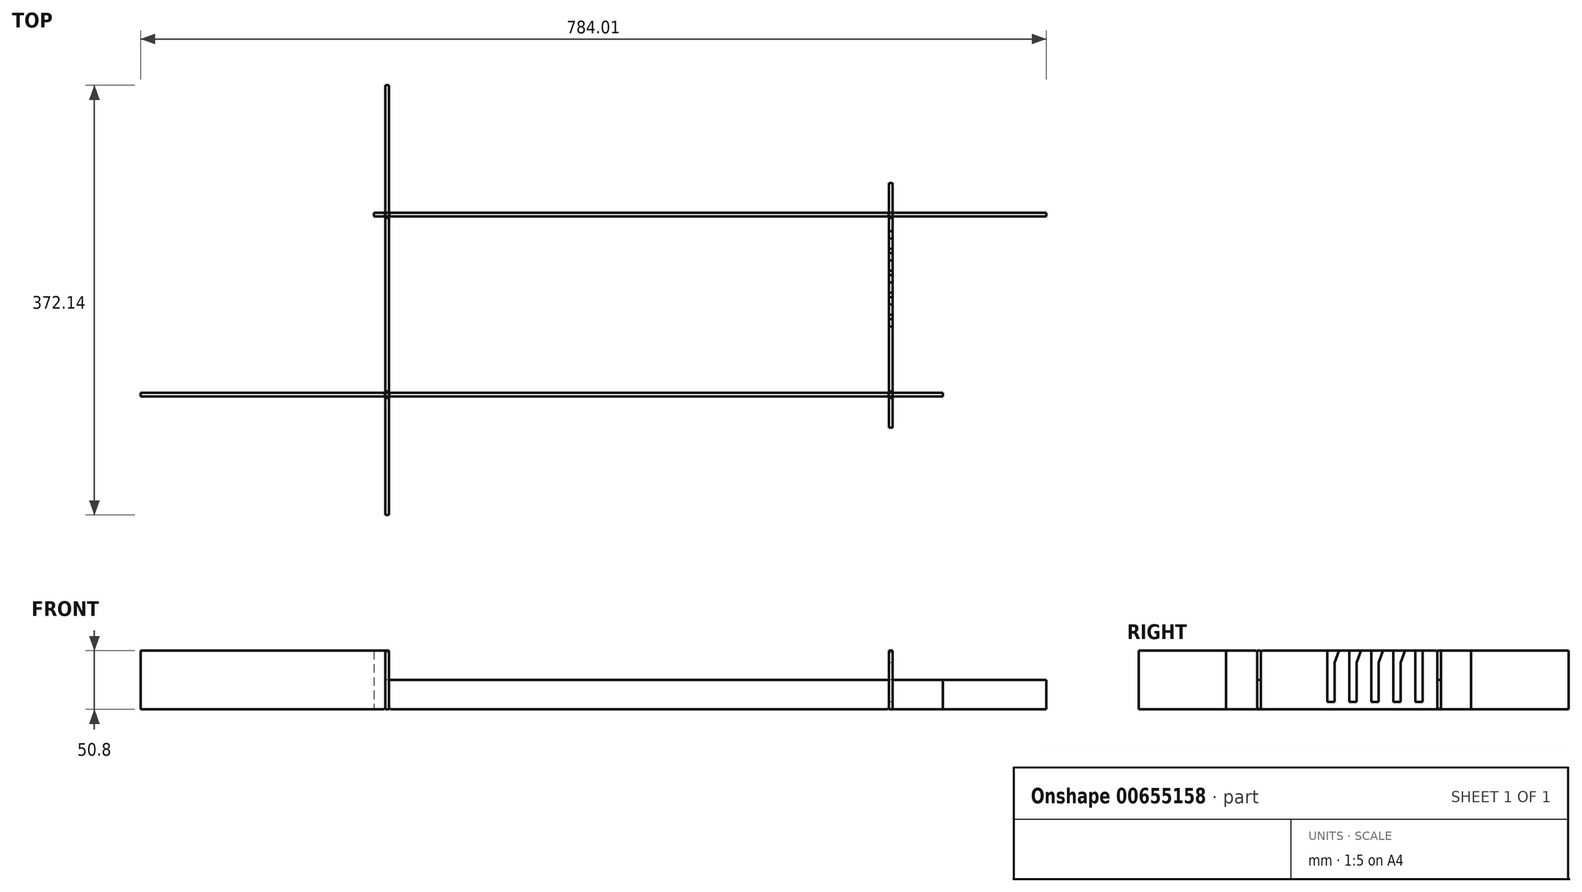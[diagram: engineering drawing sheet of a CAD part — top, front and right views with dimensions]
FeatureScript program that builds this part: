
annotation { "Feature Type Name" : "Feature", "Feature Type Description" : "" }
export const myFeature = defineFeature(function(context is Context, id is Id, definition is map)
    precondition{}
    {
        {
            var Q0;
            Q0=qCreatedBy(makeId("Top.planeOp"),FACE);
            var sketch = newSketch(context, id + "F0", { "sketchPlane" : qUnion([Q0])});
            skLineSegment(sketch, "E0", {"start": v(-96.66, -0.18) * mm, "end": v(55.66, 4.68) * mm, "construction": true});
            skLineSegment(sketch, "E1.bottom", {"start": v(-88.9, 247.87) * mm, "end": v(-85.73, 247.87) * mm});
            skLineSegment(sketch, "E1.top", {"start": v(-88.9, -124.27) * mm, "end": v(-85.72, -124.27) * mm});
            skLineSegment(sketch, "E1.left", {"start": v(-88.9, 247.87) * mm, "end": v(-88.9, -124.27) * mm});
            skLineSegment(sketch, "E1.right", {"start": v(-85.73, 247.87) * mm, "end": v(-85.72, -124.27) * mm});
            skLineSegment(sketch, "E2.bottom", {"start": v(-300.84, -18.6) * mm, "end": v(393.7, -18.6) * mm});
            skLineSegment(sketch, "E2.top", {"start": v(-300.84, -21.78) * mm, "end": v(393.7, -21.78) * mm});
            skLineSegment(sketch, "E2.left", {"start": v(-300.84, -18.6) * mm, "end": v(-300.84, -21.78) * mm});
            skLineSegment(sketch, "E2.right", {"start": v(393.7, -18.6) * mm, "end": v(393.7, -21.78) * mm});
            skLineSegment(sketch, "E3.bottom", {"start": v(483.17, 134.22) * mm, "end": v(-98.96, 134.22) * mm});
            skLineSegment(sketch, "E3.top", {"start": v(483.17, 137.4) * mm, "end": v(-98.96, 137.4) * mm});
            skLineSegment(sketch, "E3.left", {"start": v(483.17, 134.22) * mm, "end": v(483.17, 137.4) * mm});
            skLineSegment(sketch, "E3.right", {"start": v(-98.96, 134.22) * mm, "end": v(-98.96, 137.4) * mm});
            skLineSegment(sketch, "E4.bottom", {"start": v(350.04, -48.6) * mm, "end": v(346.87, -48.6) * mm});
            skLineSegment(sketch, "E4.top", {"start": v(350.04, 163.24) * mm, "end": v(346.87, 163.24) * mm});
            skLineSegment(sketch, "E4.left", {"start": v(350.04, -48.6) * mm, "end": v(350.04, 163.24) * mm});
            skLineSegment(sketch, "E4.right", {"start": v(346.87, -48.6) * mm, "end": v(346.87, 163.24) * mm});
            skSolve(sketch);
        }
        {
            var Q0;
            {var subQ0=sQuery(id+"F0.wireOp",EDGE,"E1.bottom");Q0=makeQuery(id+"F0.imprint","IMPRINT",FACE,{"disambiguationData":[TD([[makeQuery(id+"F0.imprint","IMPRINT",EDGE,{"derivedFrom":subQ0}),-1.0]])]});}
            var Q1;
            {var subQ0=sQuery(id+"F0.wireOp",EDGE,"E1.top");Q1=makeQuery(id+"F0.imprint","IMPRINT",FACE,{"disambiguationData":[TD([[makeQuery(id+"F0.imprint","IMPRINT",EDGE,{"derivedFrom":subQ0}),1.0]])]});}
            var Q2;
            {var subQ0=sQuery(id+"F0.wireOp",EDGE,"E2.bottom");var subQ1=sQuery(id+"F0.wireOp",EDGE,"E1.left");var subQ2=makeQuery(id+"F0.imprint","INTERSECT",VERTEX,{"derivedFrom":[subQ1,subQ0]});Q2=makeQuery(id+"F0.imprint","IMPRINT",FACE,{"disambiguationData":[TD([[makeQuery(id+"F0.imprint","IMPRINT",EDGE,{"disambiguationData":[TD([[subQ2,-1.0]])],"derivedFrom":subQ1}),1.0]])]});}
            var Q3;
            {var subQ0=sQuery(id+"F0.wireOp",EDGE,"E3.top");var subQ1=sQuery(id+"F0.wireOp",EDGE,"E1.left");var subQ2=makeQuery(id+"F0.imprint","INTERSECT",VERTEX,{"derivedFrom":[subQ1,subQ0]});Q3=makeQuery(id+"F0.imprint","IMPRINT",FACE,{"disambiguationData":[TD([[makeQuery(id+"F0.imprint","IMPRINT",EDGE,{"disambiguationData":[TD([[subQ2,-1.0]])],"derivedFrom":subQ1}),1.0]])]});}
            var Q4;
            {var subQ0=sQuery(id+"F0.wireOp",EDGE,"E3.bottom");var subQ1=sQuery(id+"F0.wireOp",EDGE,"E1.left");var subQ2=makeQuery(id+"F0.imprint","INTERSECT",VERTEX,{"derivedFrom":[subQ1,subQ0]});Q4=makeQuery(id+"F0.imprint","IMPRINT",FACE,{"disambiguationData":[TD([[makeQuery(id+"F0.imprint","IMPRINT",EDGE,{"disambiguationData":[TD([[subQ2,-1.0]])],"derivedFrom":subQ1}),1.0]])]});}
            extrude(context, id + "F1", {"entities" : qUnion([Q0, Q1, Q2, Q3, Q4]), "depth" : 50.8 * mm, "offsetDistance" : 25.4 * mm});
        }
        {
            var Q0;
            {var subQ5=sQuery(id+"F0.wireOp",EDGE,"E2.left");Q0=makeQuery(id+"F0.imprint","IMPRINT",FACE,{"disambiguationData":[TD([[makeQuery(id+"F0.imprint","IMPRINT",EDGE,{"derivedFrom":subQ5}),1.0]])]});}
            var Q1;
            {var subQ0=sQuery(id+"F0.wireOp",EDGE,"E2.bottom");var subQ1=sQuery(id+"F0.wireOp",EDGE,"E1.right");var subQ2=makeQuery(id+"F0.imprint","INTERSECT",VERTEX,{"derivedFrom":[subQ1,subQ0]});Q1=makeQuery(id+"F0.imprint","IMPRINT",FACE,{"disambiguationData":[TD([[makeQuery(id+"F0.imprint","IMPRINT",EDGE,{"disambiguationData":[TD([[subQ2,-1.0]])],"derivedFrom":subQ1}),1.0]])]});}
            var Q2;
            {var subQ0=sQuery(id+"F0.wireOp",EDGE,"E2.bottom");var subQ1=sQuery(id+"F0.wireOp",EDGE,"E1.left");var subQ2=makeQuery(id+"F0.imprint","INTERSECT",VERTEX,{"derivedFrom":[subQ1,subQ0]});Q2=makeQuery(id+"F0.imprint","IMPRINT",FACE,{"disambiguationData":[TD([[makeQuery(id+"F0.imprint","IMPRINT",EDGE,{"disambiguationData":[TD([[subQ2,-1.0]])],"derivedFrom":subQ1}),1.0]])]});}
            var Q3;
            {var subQ0=sQuery(id+"F0.wireOp",EDGE,"E4.right");var subQ1=sQuery(id+"F0.wireOp",EDGE,"E2.bottom");var subQ2=makeQuery(id+"F0.imprint","INTERSECT",VERTEX,{"derivedFrom":[subQ1,subQ0]});Q3=makeQuery(id+"F0.imprint","IMPRINT",FACE,{"disambiguationData":[TD([[makeQuery(id+"F0.imprint","IMPRINT",EDGE,{"disambiguationData":[TD([[subQ2,-1.0]])],"derivedFrom":subQ1}),-1.0]])]});}
            var Q4;
            {var subQ0=sQuery(id+"F0.wireOp",EDGE,"E2.right");Q4=makeQuery(id+"F0.imprint","IMPRINT",FACE,{"disambiguationData":[TD([[makeQuery(id+"F0.imprint","IMPRINT",EDGE,{"derivedFrom":subQ0}),-1.0]])]});}
            extrude(context, id + "F2", {"entities" : qUnion([Q0, Q1, Q2, Q3, Q4]), "depth" : 50.8 * mm, "offsetDistance" : 25.4 * mm});
        }
        {
            var Q0;
            {var subQ5=sQuery(id+"F0.wireOp",EDGE,"E4.bottom");Q0=makeQuery(id+"F0.imprint","IMPRINT",FACE,{"disambiguationData":[TD([[makeQuery(id+"F0.imprint","IMPRINT",EDGE,{"derivedFrom":subQ5}),-1.0]])]});}
            var Q1;
            {var subQ0=sQuery(id+"F0.wireOp",EDGE,"E4.right");var subQ1=sQuery(id+"F0.wireOp",EDGE,"E2.bottom");var subQ2=makeQuery(id+"F0.imprint","INTERSECT",VERTEX,{"derivedFrom":[subQ1,subQ0]});Q1=makeQuery(id+"F0.imprint","IMPRINT",FACE,{"disambiguationData":[TD([[makeQuery(id+"F0.imprint","IMPRINT",EDGE,{"disambiguationData":[TD([[subQ2,-1.0]])],"derivedFrom":subQ1}),-1.0]])]});}
            var Q2;
            {var subQ0=sQuery(id+"F0.wireOp",EDGE,"E4.right");var subQ1=sQuery(id+"F0.wireOp",EDGE,"E2.bottom");var subQ2=makeQuery(id+"F0.imprint","INTERSECT",VERTEX,{"derivedFrom":[subQ1,subQ0]});Q2=makeQuery(id+"F0.imprint","IMPRINT",FACE,{"disambiguationData":[TD([[makeQuery(id+"F0.imprint","IMPRINT",EDGE,{"disambiguationData":[TD([[subQ2,-1.0]])],"derivedFrom":subQ1}),1.0]])]});}
            var Q3;
            {var subQ0=sQuery(id+"F0.wireOp",EDGE,"E4.left");var subQ1=sQuery(id+"F0.wireOp",EDGE,"E3.bottom");var subQ2=makeQuery(id+"F0.imprint","INTERSECT",VERTEX,{"derivedFrom":[subQ1,subQ0]});Q3=makeQuery(id+"F0.imprint","IMPRINT",FACE,{"disambiguationData":[TD([[makeQuery(id+"F0.imprint","IMPRINT",EDGE,{"disambiguationData":[TD([[subQ2,-1.0]])],"derivedFrom":subQ1}),-1.0]])]});}
            var Q4;
            {var subQ5=sQuery(id+"F0.wireOp",EDGE,"E4.top");Q4=makeQuery(id+"F0.imprint","IMPRINT",FACE,{"disambiguationData":[TD([[makeQuery(id+"F0.imprint","IMPRINT",EDGE,{"derivedFrom":subQ5}),1.0]])]});}
            extrude(context, id + "F3", {"entities" : qUnion([Q0, Q1, Q2, Q3, Q4]), "depth" : 50.8 * mm, "offsetDistance" : 25.4 * mm});
        }
        {
            var Q0;
            {var subQ0=sQuery(id+"F0.wireOp",EDGE,"E3.left");Q0=makeQuery(id+"F0.imprint","IMPRINT",FACE,{"disambiguationData":[TD([[makeQuery(id+"F0.imprint","IMPRINT",EDGE,{"derivedFrom":subQ0}),1.0]])]});}
            var Q1;
            {var subQ0=sQuery(id+"F0.wireOp",EDGE,"E3.right");Q1=makeQuery(id+"F0.imprint","IMPRINT",FACE,{"disambiguationData":[TD([[makeQuery(id+"F0.imprint","IMPRINT",EDGE,{"derivedFrom":subQ0}),-1.0]])]});}
            var Q2;
            {var subQ0=sQuery(id+"F0.wireOp",EDGE,"E3.top");var subQ1=sQuery(id+"F0.wireOp",EDGE,"E1.left");var subQ2=makeQuery(id+"F0.imprint","INTERSECT",VERTEX,{"derivedFrom":[subQ1,subQ0]});Q2=makeQuery(id+"F0.imprint","IMPRINT",FACE,{"disambiguationData":[TD([[makeQuery(id+"F0.imprint","IMPRINT",EDGE,{"disambiguationData":[TD([[subQ2,-1.0]])],"derivedFrom":subQ1}),1.0]])]});}
            var Q3;
            {var subQ0=sQuery(id+"F0.wireOp",EDGE,"E3.top");var subQ1=sQuery(id+"F0.wireOp",EDGE,"E1.right");var subQ2=makeQuery(id+"F0.imprint","INTERSECT",VERTEX,{"derivedFrom":[subQ1,subQ0]});Q3=makeQuery(id+"F0.imprint","IMPRINT",FACE,{"disambiguationData":[TD([[makeQuery(id+"F0.imprint","IMPRINT",EDGE,{"disambiguationData":[TD([[subQ2,-1.0]])],"derivedFrom":subQ1}),1.0]])]});}
            var Q4;
            {var subQ0=sQuery(id+"F0.wireOp",EDGE,"E4.left");var subQ1=sQuery(id+"F0.wireOp",EDGE,"E3.bottom");var subQ2=makeQuery(id+"F0.imprint","INTERSECT",VERTEX,{"derivedFrom":[subQ1,subQ0]});Q4=makeQuery(id+"F0.imprint","IMPRINT",FACE,{"disambiguationData":[TD([[makeQuery(id+"F0.imprint","IMPRINT",EDGE,{"disambiguationData":[TD([[subQ2,-1.0]])],"derivedFrom":subQ1}),-1.0]])]});}
            extrude(context, id + "F4", {"entities" : qUnion([Q0, Q1, Q2, Q3, Q4]), "depth" : 50.8 * mm, "offsetDistance" : 25.4 * mm});
        }
        {
            var Q0;
            Q0=makeQuery(id+"F1.opExtrude","SWEPT_FACE",FACE,{"disambiguationData":[OSD([sQuery(id+"F0.wireOp",EDGE,"E1.left")])]});
            var sketch = newSketch(context, id + "F5", { "sketchPlane" : qUnion([Q0])});
            skLineSegment(sketch, "E5.bottom", {"start": v(-137.4, 50.8) * mm, "end": v(-134.22, 50.8) * mm});
            skLineSegment(sketch, "E5.top", {"start": v(-137.4, 25.4) * mm, "end": v(-134.22, 25.4) * mm});
            skLineSegment(sketch, "E5.left", {"start": v(-137.4, 50.8) * mm, "end": v(-137.4, 25.4) * mm});
            skLineSegment(sketch, "E5.right", {"start": v(-134.22, 50.8) * mm, "end": v(-134.22, 25.4) * mm});
            skLineSegment(sketch, "E6.bottom", {"start": v(21.78, 50.8) * mm, "end": v(18.6, 50.8) * mm});
            skLineSegment(sketch, "E6.top", {"start": v(21.78, 25.4) * mm, "end": v(18.6, 25.4) * mm});
            skLineSegment(sketch, "E6.left", {"start": v(21.78, 50.8) * mm, "end": v(21.78, 25.4) * mm});
            skLineSegment(sketch, "E6.right", {"start": v(18.6, 50.8) * mm, "end": v(18.6, 25.4) * mm});
            skSolve(sketch);
        }
        {
            var Q0;
            Q0 = qSketchRegion(id + "F5", true);
            extrude(context, id + "F6", {"entities" : qUnion([Q0]), "operationType" : NewBodyOperationType.REMOVE, "endBound" : BoundingType.THROUGH_ALL, "oppositeDirection" : true, "depth" : 25.4 * mm, "offsetDistance" : 25.4 * mm});
        }
        {
            var Q0;
            Q0=makeQuery(id+"F1.opExtrude","SWEPT_BODY",BODY,{"disambiguationData":[OSD([sQuery(id+"F0.wireOp",EDGE,"E1.bottom"),sQuery(id+"F0.wireOp",EDGE,"E1.top"),sQuery(id+"F0.wireOp",EDGE,"E1.left"),sQuery(id+"F0.wireOp",EDGE,"E1.right")])]});
            var Q1;
            Q1=makeQuery(id+"F3.opExtrude","SWEPT_BODY",BODY,{"disambiguationData":[OSD([sQuery(id+"F0.wireOp",EDGE,"E4.bottom"),sQuery(id+"F0.wireOp",EDGE,"E4.top"),sQuery(id+"F0.wireOp",EDGE,"E4.left"),sQuery(id+"F0.wireOp",EDGE,"E4.right")])]});
            var Q2;
            Q2=makeQuery(id+"F2.opExtrude","SWEPT_BODY",BODY,{"disambiguationData":[OSD([sQuery(id+"F0.wireOp",EDGE,"E2.bottom"),sQuery(id+"F0.wireOp",EDGE,"E2.top"),sQuery(id+"F0.wireOp",EDGE,"E2.left"),sQuery(id+"F0.wireOp",EDGE,"E2.right")])]});
            var Q3;
            Q3=makeQuery(id+"F4.opExtrude","SWEPT_BODY",BODY,{"disambiguationData":[OSD([sQuery(id+"F0.wireOp",EDGE,"E3.bottom"),sQuery(id+"F0.wireOp",EDGE,"E3.top"),sQuery(id+"F0.wireOp",EDGE,"E3.left"),sQuery(id+"F0.wireOp",EDGE,"E3.right")])]});
            var Q4;
            Q4=makeQuery(id+"F6.boolean.opBoolean","COPY",FACE,{"disambiguationData":[TD([makeQuery(id+"F1.opExtrude","SWEPT_FACE",FACE,{"disambiguationData":[OSD([sQuery(id+"F0.wireOp",EDGE,"E1.left")])]})])],"derivedFrom":makeQuery(id+"F6.opExtrude","SWEPT_FACE",FACE,{"disambiguationData":[OSD([sQuery(id+"F5.wireOp",EDGE,"E6.top")])]})});
            var Q5;
            Q5=makeQuery(id+"F6.boolean.opBoolean","COPY",FACE,{"disambiguationData":[TD([makeQuery(id+"F1.opExtrude","SWEPT_FACE",FACE,{"disambiguationData":[OSD([sQuery(id+"F0.wireOp",EDGE,"E1.left")])]})])],"derivedFrom":makeQuery(id+"F6.opExtrude","SWEPT_FACE",FACE,{"disambiguationData":[OSD([sQuery(id+"F5.wireOp",EDGE,"E5.top")])]})});
            var Q6;
            Q6=makeQuery(id+"F6.boolean.opBoolean","COPY",FACE,{"disambiguationData":[TD([makeQuery(id+"F3.opExtrude","SWEPT_FACE",FACE,{"disambiguationData":[OSD([sQuery(id+"F0.wireOp",EDGE,"E4.left")])]})])],"derivedFrom":makeQuery(id+"F6.opExtrude","SWEPT_FACE",FACE,{"disambiguationData":[OSD([sQuery(id+"F5.wireOp",EDGE,"E6.top")])]})});
            var Q7;
            Q7=makeQuery(id+"F6.boolean.opBoolean","COPY",FACE,{"disambiguationData":[TD([makeQuery(id+"F3.opExtrude","SWEPT_FACE",FACE,{"disambiguationData":[OSD([sQuery(id+"F0.wireOp",EDGE,"E4.left")])]})])],"derivedFrom":makeQuery(id+"F6.opExtrude","SWEPT_FACE",FACE,{"disambiguationData":[OSD([sQuery(id+"F5.wireOp",EDGE,"E5.top")])]})});
            booleanBodies(context, id + "F7", {"operationType" : BooleanOperationType.SUBTRACTION, "tools" : qUnion([Q0, Q1]), "targets" : qUnion([Q2, Q3]), "offset" : true, "entitiesToOffset" : qUnion([Q4, Q5, Q6, Q7]), "offsetDistance" : 0.25 * mm, "keepTools" : true});
        }
        {
            var Q0;
            Q0=makeQuery(id+"F3.opExtrude","SWEPT_FACE",FACE,{"disambiguationData":[OSD([sQuery(id+"F0.wireOp",EDGE,"E4.right")])]});
            var sketch = newSketch(context, id + "F8", { "sketchPlane" : qUnion([Q0])});
            skLineSegment(sketch, "E7.bottom", {"start": v(-121.52, 50.8) * mm, "end": v(-115.17, 50.8) * mm});
            skLineSegment(sketch, "E7.top", {"start": v(-121.52, 6.35) * mm, "end": v(-115.17, 6.35) * mm});
            skLineSegment(sketch, "E7.left", {"start": v(-121.52, 50.8) * mm, "end": v(-121.52, 6.35) * mm});
            skLineSegment(sketch, "E7.right", {"start": v(-115.17, 50.8) * mm, "end": v(-115.17, 6.35) * mm});
            skLineSegment(sketch, "E8.1.0.0", {"start": v(-102.47, 50.8) * mm, "end": v(-102.47, 6.35) * mm});
            skLineSegment(sketch, "E8.1.0.1", {"start": v(-96.12, 50.8) * mm, "end": v(-96.12, 6.35) * mm});
            skLineSegment(sketch, "E8.1.0.2", {"start": v(-102.47, 50.8) * mm, "end": v(-96.12, 50.8) * mm});
            skLineSegment(sketch, "E8.1.0.3", {"start": v(-102.47, 6.35) * mm, "end": v(-96.12, 6.35) * mm});
            skLineSegment(sketch, "E8.2.0.0", {"start": v(-83.42, 50.8) * mm, "end": v(-83.42, 6.35) * mm});
            skLineSegment(sketch, "E8.2.0.1", {"start": v(-77.07, 50.8) * mm, "end": v(-77.07, 6.35) * mm});
            skLineSegment(sketch, "E8.2.0.2", {"start": v(-83.42, 50.8) * mm, "end": v(-77.07, 50.8) * mm});
            skLineSegment(sketch, "E8.2.0.3", {"start": v(-83.42, 6.35) * mm, "end": v(-77.07, 6.35) * mm});
            skLineSegment(sketch, "E8.direction1", {"start": v(-121.52, 6.35) * mm, "end": v(-102.47, 6.35) * mm, "construction": true});
            skLineSegment(sketch, "E9.0.3.0", {"start": v(-64.37, 50.8) * mm, "end": v(-64.37, 6.35) * mm});
            skLineSegment(sketch, "E9.3.3.0", {"start": v(-58.02, 50.8) * mm, "end": v(-58.02, 6.35) * mm});
            skLineSegment(sketch, "E9.6.3.0", {"start": v(-64.37, 50.8) * mm, "end": v(-58.02, 50.8) * mm});
            skLineSegment(sketch, "E9.9.3.0", {"start": v(-64.37, 6.35) * mm, "end": v(-58.02, 6.35) * mm});
            skLineSegment(sketch, "E9.0.4.0", {"start": v(-45.32, 50.8) * mm, "end": v(-45.32, 6.35) * mm});
            skLineSegment(sketch, "E9.3.4.0", {"start": v(-38.97, 50.8) * mm, "end": v(-38.97, 6.35) * mm});
            skLineSegment(sketch, "E9.6.4.0", {"start": v(-45.32, 50.8) * mm, "end": v(-38.97, 50.8) * mm});
            skLineSegment(sketch, "E9.9.4.0", {"start": v(-45.32, 6.35) * mm, "end": v(-38.97, 6.35) * mm});
            skSolve(sketch);
        }
        {
            var Q0;
            Q0=makeQuery(id+"F8.imprint","IMPRINT",FACE,{"disambiguationData":[TD([[makeQuery(id+"F8.imprint","IMPRINT",EDGE,{"derivedFrom":sQuery(id+"F8.wireOp",EDGE,"E7.bottom")}),1.0]])]});
            var Q1;
            Q1=makeQuery(id+"F8.imprint","IMPRINT",FACE,{"disambiguationData":[TD([[makeQuery(id+"F8.imprint","IMPRINT",EDGE,{"derivedFrom":sQuery(id+"F8.wireOp",EDGE,"E8.1.0.0")}),1.0]])]});
            var Q2;
            Q2=makeQuery(id+"F8.imprint","IMPRINT",FACE,{"disambiguationData":[TD([[makeQuery(id+"F8.imprint","IMPRINT",EDGE,{"derivedFrom":sQuery(id+"F8.wireOp",EDGE,"E8.2.0.0")}),1.0]])]});
            var Q3;
            Q3=makeQuery(id+"F8.imprint","IMPRINT",FACE,{"disambiguationData":[TD([[makeQuery(id+"F8.imprint","IMPRINT",EDGE,{"derivedFrom":sQuery(id+"F8.wireOp",EDGE,"E9.0.3.0")}),1.0]])]});
            var Q4;
            Q4=makeQuery(id+"F8.imprint","IMPRINT",FACE,{"disambiguationData":[TD([[makeQuery(id+"F8.imprint","IMPRINT",EDGE,{"derivedFrom":sQuery(id+"F8.wireOp",EDGE,"E9.0.4.0")}),1.0]])]});
            extrude(context, id + "F9", {"entities" : qUnion([Q0, Q1, Q2, Q3, Q4]), "operationType" : NewBodyOperationType.REMOVE, "endBound" : BoundingType.UP_TO_NEXT, "oppositeDirection" : true, "depth" : 25.4 * mm, "offsetDistance" : 25.4 * mm});
        }
        {
            var Q0;
            Q0=makeQuery(id+"F9.boolean.opBoolean","COPY",EDGE,{"derivedFrom":makeQuery(id+"F9.opExtrude","SWEPT_EDGE",EDGE,{"disambiguationData":[OSD([sQuery(id+"F0.wireOp",EDGE,"E4.right"),sQuery(id+"F8.wireOp",EDGE,"E7.bottom"),sQuery(id+"F8.wireOp",EDGE,"E7.left")])]})});
            var Q1;
            Q1=makeQuery(id+"F9.boolean.opBoolean","COPY",EDGE,{"derivedFrom":makeQuery(id+"F9.opExtrude","SWEPT_EDGE",EDGE,{"disambiguationData":[OSD([sQuery(id+"F0.wireOp",EDGE,"E4.right"),sQuery(id+"F8.wireOp",EDGE,"E8.2.0.0"),sQuery(id+"F8.wireOp",EDGE,"E8.2.0.2")])]})});
            var Q2;
            Q2=makeQuery(id+"F9.boolean.opBoolean","COPY",EDGE,{"derivedFrom":makeQuery(id+"F9.opExtrude","SWEPT_EDGE",EDGE,{"disambiguationData":[OSD([sQuery(id+"F0.wireOp",EDGE,"E4.right"),sQuery(id+"F8.wireOp",EDGE,"E9.0.3.0"),sQuery(id+"F8.wireOp",EDGE,"E9.6.3.0")])]})});
            var Q3;
            Q3=makeQuery(id+"F9.boolean.opBoolean","COPY",EDGE,{"derivedFrom":makeQuery(id+"F9.opExtrude","SWEPT_EDGE",EDGE,{"disambiguationData":[OSD([sQuery(id+"F0.wireOp",EDGE,"E4.right"),sQuery(id+"F8.wireOp",EDGE,"E9.0.4.0"),sQuery(id+"F8.wireOp",EDGE,"E9.6.4.0")])]})});
            var Q4;
            Q4=makeQuery(id+"F9.boolean.opBoolean","COPY",EDGE,{"derivedFrom":makeQuery(id+"F9.opExtrude","SWEPT_EDGE",EDGE,{"disambiguationData":[OSD([sQuery(id+"F0.wireOp",EDGE,"E4.right"),sQuery(id+"F8.wireOp",EDGE,"E8.1.0.0"),sQuery(id+"F8.wireOp",EDGE,"E8.1.0.2")])]})});
            chamfer(context, id + "F10", {"entities" : qUnion([Q0, Q1, Q2, Q3, Q4]), "chamferType" : ChamferType.OFFSET_ANGLE, "width" : 3.8 * mm, "oppositeDirection" : true, "angle" : 70 * degree, "tangentPropagation" : true});
        }
        {
            var Q0;
            {var subQ0=sQuery(id+"F5.wireOp",EDGE,"E5.right");Q0=makeQuery(id+"F6.boolean.opBoolean","COPY",EDGE,{"disambiguationData":[topologyDisambiguationEdgeConnected([makeQuery(id+"F3.opExtrude","CAP_FACE",FACE,{"disambiguationData":[OSD([sQuery(id+"F0.wireOp",EDGE,"E4.bottom"),sQuery(id+"F0.wireOp",EDGE,"E4.top"),sQuery(id+"F0.wireOp",EDGE,"E4.left"),sQuery(id+"F0.wireOp",EDGE,"E4.right")])],"isStart":false})])],"derivedFrom":makeQuery(id+"F6.opExtrude","SWEPT_EDGE",EDGE,{"disambiguationData":[OSD([sQuery(id+"F0.wireOp",EDGE,"E1.left"),sQuery(id+"F5.wireOp",EDGE,"E5.bottom"),subQ0])]})});}
            var Q1;
            {var subQ0=sQuery(id+"F5.wireOp",EDGE,"E5.left");Q1=makeQuery(id+"F6.boolean.opBoolean","COPY",EDGE,{"disambiguationData":[topologyDisambiguationEdgeConnected([makeQuery(id+"F3.opExtrude","CAP_FACE",FACE,{"disambiguationData":[OSD([sQuery(id+"F0.wireOp",EDGE,"E4.bottom"),sQuery(id+"F0.wireOp",EDGE,"E4.top"),sQuery(id+"F0.wireOp",EDGE,"E4.left"),sQuery(id+"F0.wireOp",EDGE,"E4.right")])],"isStart":false})])],"derivedFrom":makeQuery(id+"F6.opExtrude","SWEPT_EDGE",EDGE,{"disambiguationData":[OSD([sQuery(id+"F0.wireOp",EDGE,"E1.left"),sQuery(id+"F5.wireOp",EDGE,"E5.bottom"),subQ0])]})});}
            var Q2;
            {var subQ0=sQuery(id+"F5.wireOp",EDGE,"E6.left");Q2=makeQuery(id+"F6.boolean.opBoolean","COPY",EDGE,{"disambiguationData":[topologyDisambiguationEdgeConnected([makeQuery(id+"F3.opExtrude","CAP_FACE",FACE,{"disambiguationData":[OSD([sQuery(id+"F0.wireOp",EDGE,"E4.bottom"),sQuery(id+"F0.wireOp",EDGE,"E4.top"),sQuery(id+"F0.wireOp",EDGE,"E4.left"),sQuery(id+"F0.wireOp",EDGE,"E4.right")])],"isStart":false})])],"derivedFrom":makeQuery(id+"F6.opExtrude","SWEPT_EDGE",EDGE,{"disambiguationData":[OSD([sQuery(id+"F0.wireOp",EDGE,"E1.left"),sQuery(id+"F5.wireOp",EDGE,"E6.bottom"),subQ0])]})});}
            var Q3;
            {var subQ0=sQuery(id+"F5.wireOp",EDGE,"E6.right");Q3=makeQuery(id+"F6.boolean.opBoolean","COPY",EDGE,{"disambiguationData":[topologyDisambiguationEdgeConnected([makeQuery(id+"F3.opExtrude","CAP_FACE",FACE,{"disambiguationData":[OSD([sQuery(id+"F0.wireOp",EDGE,"E4.bottom"),sQuery(id+"F0.wireOp",EDGE,"E4.top"),sQuery(id+"F0.wireOp",EDGE,"E4.left"),sQuery(id+"F0.wireOp",EDGE,"E4.right")])],"isStart":false})])],"derivedFrom":makeQuery(id+"F6.opExtrude","SWEPT_EDGE",EDGE,{"disambiguationData":[OSD([sQuery(id+"F0.wireOp",EDGE,"E1.left"),sQuery(id+"F5.wireOp",EDGE,"E6.bottom"),subQ0])]})});}
            var Q4;
            {var subQ0=sQuery(id+"F0.wireOp",EDGE,"E1.left");var subQ1=sQuery(id+"F5.wireOp",EDGE,"E5.right");Q4=makeQuery(id+"F6.boolean.opBoolean","COPY",EDGE,{"disambiguationData":[topologyDisambiguationEdgeConnected([makeQuery(id+"F1.opExtrude","CAP_FACE",FACE,{"disambiguationData":[OSD([sQuery(id+"F0.wireOp",EDGE,"E1.bottom"),sQuery(id+"F0.wireOp",EDGE,"E1.top"),subQ0,sQuery(id+"F0.wireOp",EDGE,"E1.right")])],"isStart":false})])],"derivedFrom":makeQuery(id+"F6.opExtrude","SWEPT_EDGE",EDGE,{"disambiguationData":[OSD([subQ0,sQuery(id+"F5.wireOp",EDGE,"E5.bottom"),subQ1])]})});}
            var Q5;
            {var subQ0=sQuery(id+"F0.wireOp",EDGE,"E1.left");var subQ1=sQuery(id+"F5.wireOp",EDGE,"E5.left");Q5=makeQuery(id+"F6.boolean.opBoolean","COPY",EDGE,{"disambiguationData":[topologyDisambiguationEdgeConnected([makeQuery(id+"F1.opExtrude","CAP_FACE",FACE,{"disambiguationData":[OSD([sQuery(id+"F0.wireOp",EDGE,"E1.bottom"),sQuery(id+"F0.wireOp",EDGE,"E1.top"),subQ0,sQuery(id+"F0.wireOp",EDGE,"E1.right")])],"isStart":false})])],"derivedFrom":makeQuery(id+"F6.opExtrude","SWEPT_EDGE",EDGE,{"disambiguationData":[OSD([subQ0,sQuery(id+"F5.wireOp",EDGE,"E5.bottom"),subQ1])]})});}
            var Q6;
            {var subQ0=sQuery(id+"F0.wireOp",EDGE,"E1.left");var subQ1=sQuery(id+"F5.wireOp",EDGE,"E6.left");Q6=makeQuery(id+"F6.boolean.opBoolean","COPY",EDGE,{"disambiguationData":[topologyDisambiguationEdgeConnected([makeQuery(id+"F1.opExtrude","CAP_FACE",FACE,{"disambiguationData":[OSD([sQuery(id+"F0.wireOp",EDGE,"E1.bottom"),sQuery(id+"F0.wireOp",EDGE,"E1.top"),subQ0,sQuery(id+"F0.wireOp",EDGE,"E1.right")])],"isStart":false})])],"derivedFrom":makeQuery(id+"F6.opExtrude","SWEPT_EDGE",EDGE,{"disambiguationData":[OSD([subQ0,sQuery(id+"F5.wireOp",EDGE,"E6.bottom"),subQ1])]})});}
            var Q7;
            {var subQ0=sQuery(id+"F0.wireOp",EDGE,"E1.left");var subQ1=sQuery(id+"F5.wireOp",EDGE,"E6.right");Q7=makeQuery(id+"F6.boolean.opBoolean","COPY",EDGE,{"disambiguationData":[topologyDisambiguationEdgeConnected([makeQuery(id+"F1.opExtrude","CAP_FACE",FACE,{"disambiguationData":[OSD([sQuery(id+"F0.wireOp",EDGE,"E1.bottom"),sQuery(id+"F0.wireOp",EDGE,"E1.top"),subQ0,sQuery(id+"F0.wireOp",EDGE,"E1.right")])],"isStart":false})])],"derivedFrom":makeQuery(id+"F6.opExtrude","SWEPT_EDGE",EDGE,{"disambiguationData":[OSD([subQ0,sQuery(id+"F5.wireOp",EDGE,"E6.bottom"),subQ1])]})});}
            chamfer(context, id + "F11", {"entities" : qUnion([Q0, Q1, Q2, Q3, Q4, Q5, Q6, Q7]), "width" : 1.27 * mm, "tangentPropagation" : true});
        }
        {
            var Q0;
            {var subQ0=sQuery(id+"F0.wireOp",EDGE,"E1.left");Q0=makeQuery(id+"F7.tempBoolean.opBoolean","COPY",EDGE,{"disambiguationData":[topologyDisambiguationEdgeConnected([makeQuery(id+"F2.opExtrude","CAP_FACE",FACE,{"disambiguationData":[OSD([sQuery(id+"F0.wireOp",EDGE,"E2.bottom"),sQuery(id+"F0.wireOp",EDGE,"E2.top"),sQuery(id+"F0.wireOp",EDGE,"E2.left"),sQuery(id+"F0.wireOp",EDGE,"E2.right")])],"isStart":true})])],"derivedFrom":makeQuery(id+"F7.offsetTempBody.opPattern","COPY",EDGE,{"derivedFrom":makeQuery(id+"F1.opExtrude","CAP_EDGE",EDGE,{"disambiguationData":[OSD([subQ0])],"isStart":true}),"instanceName":"1"})});}
            var Q1;
            {var subQ0=sQuery(id+"F0.wireOp",EDGE,"E1.right");Q1=makeQuery(id+"F7.tempBoolean.opBoolean","COPY",EDGE,{"disambiguationData":[topologyDisambiguationEdgeConnected([makeQuery(id+"F2.opExtrude","CAP_FACE",FACE,{"disambiguationData":[OSD([sQuery(id+"F0.wireOp",EDGE,"E2.bottom"),sQuery(id+"F0.wireOp",EDGE,"E2.top"),sQuery(id+"F0.wireOp",EDGE,"E2.left"),sQuery(id+"F0.wireOp",EDGE,"E2.right")])],"isStart":true})])],"derivedFrom":makeQuery(id+"F7.offsetTempBody.opPattern","COPY",EDGE,{"derivedFrom":makeQuery(id+"F1.opExtrude","CAP_EDGE",EDGE,{"disambiguationData":[OSD([subQ0])],"isStart":true}),"instanceName":"1"})});}
            var Q2;
            {var subQ0=sQuery(id+"F0.wireOp",EDGE,"E4.left");Q2=makeQuery(id+"F7.tempBoolean.opBoolean","COPY",EDGE,{"disambiguationData":[topologyDisambiguationEdgeConnected([makeQuery(id+"F2.opExtrude","CAP_FACE",FACE,{"disambiguationData":[OSD([sQuery(id+"F0.wireOp",EDGE,"E2.bottom"),sQuery(id+"F0.wireOp",EDGE,"E2.top"),sQuery(id+"F0.wireOp",EDGE,"E2.left"),sQuery(id+"F0.wireOp",EDGE,"E2.right")])],"isStart":true})])],"derivedFrom":makeQuery(id+"F7.offsetTempBody.opPattern","COPY",EDGE,{"derivedFrom":makeQuery(id+"F3.opExtrude","CAP_EDGE",EDGE,{"disambiguationData":[OSD([subQ0])],"isStart":true}),"instanceName":"1"})});}
            var Q3;
            {var subQ0=sQuery(id+"F0.wireOp",EDGE,"E4.right");Q3=makeQuery(id+"F7.tempBoolean.opBoolean","COPY",EDGE,{"disambiguationData":[topologyDisambiguationEdgeConnected([makeQuery(id+"F2.opExtrude","CAP_FACE",FACE,{"disambiguationData":[OSD([sQuery(id+"F0.wireOp",EDGE,"E2.bottom"),sQuery(id+"F0.wireOp",EDGE,"E2.top"),sQuery(id+"F0.wireOp",EDGE,"E2.left"),sQuery(id+"F0.wireOp",EDGE,"E2.right")])],"isStart":true})])],"derivedFrom":makeQuery(id+"F7.offsetTempBody.opPattern","COPY",EDGE,{"derivedFrom":makeQuery(id+"F3.opExtrude","CAP_EDGE",EDGE,{"disambiguationData":[OSD([subQ0])],"isStart":true}),"instanceName":"1"})});}
            var Q4;
            {var subQ0=sQuery(id+"F0.wireOp",EDGE,"E4.left");Q4=makeQuery(id+"F7.tempBoolean.opBoolean","COPY",EDGE,{"disambiguationData":[topologyDisambiguationEdgeConnected([makeQuery(id+"F4.opExtrude","CAP_FACE",FACE,{"disambiguationData":[OSD([sQuery(id+"F0.wireOp",EDGE,"E3.bottom"),sQuery(id+"F0.wireOp",EDGE,"E3.top"),sQuery(id+"F0.wireOp",EDGE,"E3.left"),sQuery(id+"F0.wireOp",EDGE,"E3.right")])],"isStart":true})])],"derivedFrom":makeQuery(id+"F7.offsetTempBody.opPattern","COPY",EDGE,{"derivedFrom":makeQuery(id+"F3.opExtrude","CAP_EDGE",EDGE,{"disambiguationData":[OSD([subQ0])],"isStart":true}),"instanceName":"1"})});}
            var Q5;
            {var subQ0=sQuery(id+"F0.wireOp",EDGE,"E4.right");Q5=makeQuery(id+"F7.tempBoolean.opBoolean","COPY",EDGE,{"disambiguationData":[topologyDisambiguationEdgeConnected([makeQuery(id+"F4.opExtrude","CAP_FACE",FACE,{"disambiguationData":[OSD([sQuery(id+"F0.wireOp",EDGE,"E3.bottom"),sQuery(id+"F0.wireOp",EDGE,"E3.top"),sQuery(id+"F0.wireOp",EDGE,"E3.left"),sQuery(id+"F0.wireOp",EDGE,"E3.right")])],"isStart":true})])],"derivedFrom":makeQuery(id+"F7.offsetTempBody.opPattern","COPY",EDGE,{"derivedFrom":makeQuery(id+"F3.opExtrude","CAP_EDGE",EDGE,{"disambiguationData":[OSD([subQ0])],"isStart":true}),"instanceName":"1"})});}
            var Q6;
            {var subQ0=sQuery(id+"F0.wireOp",EDGE,"E1.right");Q6=makeQuery(id+"F7.tempBoolean.opBoolean","COPY",EDGE,{"disambiguationData":[topologyDisambiguationEdgeConnected([makeQuery(id+"F4.opExtrude","CAP_FACE",FACE,{"disambiguationData":[OSD([sQuery(id+"F0.wireOp",EDGE,"E3.bottom"),sQuery(id+"F0.wireOp",EDGE,"E3.top"),sQuery(id+"F0.wireOp",EDGE,"E3.left"),sQuery(id+"F0.wireOp",EDGE,"E3.right")])],"isStart":true})])],"derivedFrom":makeQuery(id+"F7.offsetTempBody.opPattern","COPY",EDGE,{"derivedFrom":makeQuery(id+"F1.opExtrude","CAP_EDGE",EDGE,{"disambiguationData":[OSD([subQ0])],"isStart":true}),"instanceName":"1"})});}
            var Q7;
            {var subQ0=sQuery(id+"F0.wireOp",EDGE,"E1.left");Q7=makeQuery(id+"F7.tempBoolean.opBoolean","COPY",EDGE,{"disambiguationData":[topologyDisambiguationEdgeConnected([makeQuery(id+"F4.opExtrude","CAP_FACE",FACE,{"disambiguationData":[OSD([sQuery(id+"F0.wireOp",EDGE,"E3.bottom"),sQuery(id+"F0.wireOp",EDGE,"E3.top"),sQuery(id+"F0.wireOp",EDGE,"E3.left"),sQuery(id+"F0.wireOp",EDGE,"E3.right")])],"isStart":true})])],"derivedFrom":makeQuery(id+"F7.offsetTempBody.opPattern","COPY",EDGE,{"derivedFrom":makeQuery(id+"F1.opExtrude","CAP_EDGE",EDGE,{"disambiguationData":[OSD([subQ0])],"isStart":true}),"instanceName":"1"})});}
            chamfer(context, id + "F12", {"entities" : qUnion([Q0, Q1, Q2, Q3, Q4, Q5, Q6, Q7]), "width" : 1.27 * mm, "tangentPropagation" : true});
        }
    });
